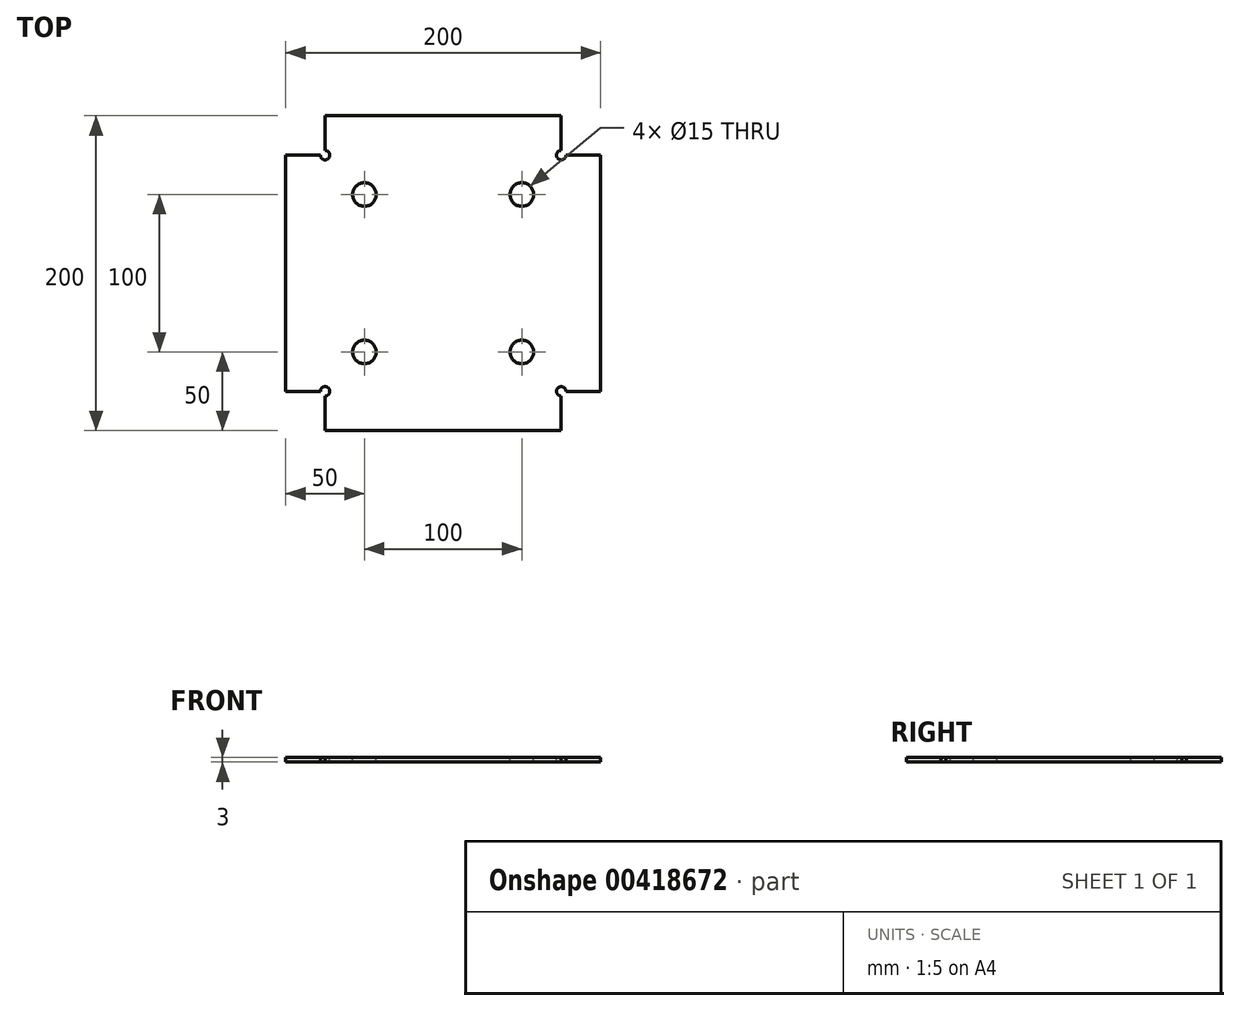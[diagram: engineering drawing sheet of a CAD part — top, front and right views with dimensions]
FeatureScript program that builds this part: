
annotation { "Feature Type Name" : "Feature", "Feature Type Description" : "" }
export const myFeature = defineFeature(function(context is Context, id is Id, definition is map)
    precondition{}
    {
        {
            var Q0;
            Q0=qCreatedBy(makeId("Top.planeOp"),FACE);
            var sketch = newSketch(context, id + "F0", { "sketchPlane" : qUnion([Q0])});
            skLineSegment(sketch, "E0.bottom", {"start": v(-100, 100) * mm, "end": v(100, 100) * mm});
            skLineSegment(sketch, "E0.top", {"start": v(-100, -100) * mm, "end": v(100, -100) * mm});
            skLineSegment(sketch, "E0.left", {"start": v(-100, 100) * mm, "end": v(-100, -100) * mm});
            skLineSegment(sketch, "E0.right", {"start": v(100, 100) * mm, "end": v(100, -100) * mm});
            skSolve(sketch);
        }
        {
            var Q0;
            Q0=makeQuery(id+"F0.imprint","IMPRINT",FACE,{"disambiguationData":[TD([[makeQuery(id+"F0.imprint","IMPRINT",EDGE,{"derivedFrom":sQuery(id+"F0.wireOp",EDGE,"E0.bottom")}),-1.0]])]});
            extrude(context, id + "F1", {"entities" : qUnion([Q0]), "depth" : 3 * mm});
        }
        {
            var Q0;
            Q0=makeQuery(id+"F1.opExtrude","CAP_FACE",FACE,{"disambiguationData":[OSD([sQuery(id+"F0.wireOp",EDGE,"E0.bottom"),sQuery(id+"F0.wireOp",EDGE,"E0.top"),sQuery(id+"F0.wireOp",EDGE,"E0.left"),sQuery(id+"F0.wireOp",EDGE,"E0.right")])],"isStart":false});
            var sketch = newSketch(context, id + "F2", { "sketchPlane" : qUnion([Q0])});
            skLineSegment(sketch, "E1", {"start": v(-100, 100) * mm, "end": v(100, -100) * mm, "construction": true});
            skLineSegment(sketch, "E2", {"start": v(-100, -100) * mm, "end": v(100, 100) * mm, "construction": true});
            skLineSegment(sketch, "E3.bottom", {"start": v(-100, 100) * mm, "end": v(-75, 100) * mm});
            skLineSegment(sketch, "E3.top", {"start": v(-100, 75) * mm, "end": v(-78, 75) * mm});
            skLineSegment(sketch, "E3.left", {"start": v(-100, 100) * mm, "end": v(-100, 75) * mm});
            skLineSegment(sketch, "E3.right", {"start": v(-75, 100) * mm, "end": v(-75, 78) * mm});
            skArc(sketch, "E4", {"start": v(-78, 75) * mm, "mid": v(-72.88, 72.88) * mm, "end": v(-75, 78) * mm});
            skArc(sketch, "E5.MirrorCS", {"start": v(78, 75) * mm, "mid": v(72.88, 72.88) * mm, "end": v(75, 78) * mm});
            skLineSegment(sketch, "E6.MirrorCS", {"start": v(100, 75) * mm, "end": v(78, 75) * mm});
            skLineSegment(sketch, "E7.MirrorCS", {"start": v(100, 100) * mm, "end": v(100, 75) * mm});
            skLineSegment(sketch, "E8.MirrorCS", {"start": v(100, 100) * mm, "end": v(75, 100) * mm});
            skLineSegment(sketch, "E9.MirrorCS", {"start": v(75, 100) * mm, "end": v(75, 78) * mm});
            skLineSegment(sketch, "E10.MirrorCS", {"start": v(-75, -100) * mm, "end": v(-75, -78) * mm});
            skArc(sketch, "E11.MirrorCS", {"start": v(78, -75) * mm, "mid": v(72.88, -72.88) * mm, "end": v(75, -78) * mm});
            skLineSegment(sketch, "E12.MirrorCS", {"start": v(-100, -100) * mm, "end": v(-75, -100) * mm});
            skArc(sketch, "E13.MirrorCS", {"start": v(-78, -75) * mm, "mid": v(-72.88, -72.88) * mm, "end": v(-75, -78) * mm});
            skLineSegment(sketch, "E14.MirrorCS", {"start": v(75, -100) * mm, "end": v(75, -78) * mm});
            skLineSegment(sketch, "E15.MirrorCS", {"start": v(-100, -100) * mm, "end": v(-100, -75) * mm});
            skLineSegment(sketch, "E16.MirrorCS", {"start": v(-100, -75) * mm, "end": v(-78, -75) * mm});
            skLineSegment(sketch, "E17.MirrorCS", {"start": v(100, -100) * mm, "end": v(75, -100) * mm});
            skLineSegment(sketch, "E18.MirrorCS", {"start": v(100, -100) * mm, "end": v(100, -75) * mm});
            skLineSegment(sketch, "E19.MirrorCS", {"start": v(100, -75) * mm, "end": v(78, -75) * mm});
            skSolve(sketch);
        }
        {
            var Q0;
            Q0 = qSketchRegion(id + "F2", true);
            extrude(context, id + "F3", {"entities" : qUnion([Q0]), "operationType" : NewBodyOperationType.REMOVE, "endBound" : BoundingType.THROUGH_ALL, "oppositeDirection" : true, "depth" : 25 * mm});
        }
        {
            var Q0;
            Q0=makeQuery(id+"F1.opExtrude","CAP_FACE",FACE,{"disambiguationData":[OSD([sQuery(id+"F0.wireOp",EDGE,"E0.bottom"),sQuery(id+"F0.wireOp",EDGE,"E0.top"),sQuery(id+"F0.wireOp",EDGE,"E0.left"),sQuery(id+"F0.wireOp",EDGE,"E0.right")])],"isStart":false});
            var sketch = newSketch(context, id + "F4", { "sketchPlane" : qUnion([Q0])});
            skCircle(sketch, "E20", {"center": v(-50, 50) * mm, "radius": 7.5 * mm});
            skCircle(sketch, "E21.MirrorC", {"center": v(50, 50) * mm, "radius": 7.5 * mm});
            skCircle(sketch, "E22.MirrorC", {"center": v(-50, -50) * mm, "radius": 7.5 * mm});
            skCircle(sketch, "E23.MirrorC", {"center": v(50, -50) * mm, "radius": 7.5 * mm});
            skSolve(sketch);
        }
        {
            var Q0;
            Q0 = qSketchRegion(id + "F4", true);
            extrude(context, id + "F5", {"entities" : qUnion([Q0]), "operationType" : NewBodyOperationType.REMOVE, "endBound" : BoundingType.THROUGH_ALL, "oppositeDirection" : true, "depth" : 25 * mm});
        }
    });
